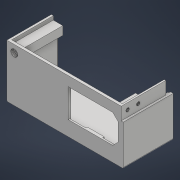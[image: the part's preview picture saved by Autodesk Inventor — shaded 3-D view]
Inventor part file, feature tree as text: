
AUTODESK INVENTOR PART (.ipt)
format: ipt  version: 2021 (Build 250183000, 183)  size: 828,416 bytes
history: native  units: mm
features: extrude x9, sketch x9, projected_geometry x7, thicken_offset x5, other x3, fillet x2, direct_edit x1, move_body x1
ambient origin geometry x8: Origin, YZ Plane, XZ Plane, XY Plane, X Axis, Y Axis, Z Axis, Center Point
bodies: Solid1 (feature_tree)
feature tree (37):
  other  "psu_cover_20a_i3_steel"
  other  "MeshFeature1"
  extrude  "Extrusion1"  Depth=10.0mm TaperAngle=0.0deg
  extrude  "Extrusion2"  Depth=27.0mm
  extrude  "Extrusion3"  Depth=6.0mm
  extrude  "Extrusion4"  Depth=5.0mm
  extrude  "Extrusion5"  Depth=5.0mm
  fillet  "Fillet1"  Radius=10.0mm
  fillet  "Fillet2"  Radius=10.0mm
  extrude  "Extrusion6"  Depth=10.0mm TaperAngle=0.0deg
  extrude  "Extrusion7"  Depth=1.0mm
  thicken_offset  "Thicken1"
  thicken_offset  "Thicken2"
  thicken_offset  "Thicken3"
  thicken_offset  "Thicken4"
  thicken_offset  "Thicken5"
  extrude  "Extrusion8"  Depth=15.0mm
  direct_edit  "Direct Edit1"
  other  "Lip1"
  extrude  "Extrusion9"  Depth=11.0mm
  sketch  "Sketch1"  dims[d0=10.0mm d1=0.0mm d2=10.0mm d3=0.0mm]
  projected_geometry  "Projected Loop1"
  sketch  "Sketch2"  dims[d4=47.0mm d5=27.0mm]
  projected_geometry  "Projected Loop2"
  sketch  "Sketch3"  dims[d6=5.0mm d7=6.0mm]
  sketch  "Sketch4"  dims[d8=5.0mm d9=5.0mm]
  projected_geometry  "Projected Loop3"
  sketch  "Sketch5"  dims[d10=5.0mm d11=5.0mm d12=10.0mm d13=0.0mm d14=10.0mm d15=0.0mm]
  projected_geometry  "Projected Loop4"
  sketch  "Sketch6"  dims[d16=14.0mm d17=10.0mm d18=0.0mm]
  projected_geometry  "Projected Loop5"
  sketch  "Sketch7"  dims[d19=3.0mm d20=1.0mm]
  projected_geometry  "Projected Loop6"
  sketch  "Sketch8"  dims[d21=1.5mm d22=15.0mm]
  projected_geometry  "Projected Loop7"
  sketch  "Sketch9"  dims[d23=15.0mm d24=11.0mm d25=11.0mm d26=1.5mm d27=0.0mm d28=10.0mm d29=0.0mm d30=1.0mm d31=1.0mm d32=0.5mm d33=0.5mm d34=0.5mm d35=0.5mm d36=1.0mm d37=1.0mm d38=1.0mm d39=1.0mm d40=10.0mm d41=0.0mm d42=0.0mm d43=0.0mm d44=-8.0mm d45=6.0mm d46=3.0mm d47=0.0mm d48=0.0mm d49=1.5mm d50=1.0mm d51=0.0mm d52=0.0mm d53=0.0mm d54=0.0mm]
  move_body  "Move1"
